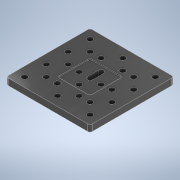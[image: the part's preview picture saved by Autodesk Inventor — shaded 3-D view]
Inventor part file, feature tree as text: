
AUTODESK INVENTOR PART (.ipt)
format: ipt  version: 2022 (Build 260153000, 153)  size: 283,136 bytes
history: native  units: mm
features: sketch x5, extrude x4, projected_geometry x1
ambient origin geometry x8: Origin, YZ Plane, XZ Plane, XY Plane, X Axis, Y Axis, Z Axis, Center Point
bodies: Solid1 (feature_tree)
feature tree (10):
  extrude  "Extrusion1"  Depth=77.0mm
  extrude  "Extrusion2"  Depth=8.5mm
  extrude  "Extrusion3"  Depth=20.0mm
  extrude  "Extrusion4"  Depth=5.0mm
  sketch  "Sketch5"  dims[d8=5.0mm d9=5.0mm d10=5.0mm d11=30.0mm d12=30.0mm d13=20.0mm d14=20.0mm d15=5.0mm d16=5.0mm d17=5.0mm d18=18.5mm d19=18.5mm d20=18.5mm d21=18.5mm d22=18.5mm d23=18.5mm d24=5.0mm d25=5.0mm d26=10.0mm d27=10.0mm d28=10.0mm d29=5.0mm d30=5.0mm d31=20.0mm d32=5.0mm d33=5.0mm d34=5.0mm d35=2.0mm d36=2.0mm d37=6.0mm d38=0.0mm d39=23.5mm d40=23.5mm d41=23.5mm d42=23.5mm d43=2.0mm d44=1.0mm d45=0.0mm d46=15.0mm d47=0.0mm d49=15.0mm d50=8.0mm d51=22.0mm d52=0.0mm d53=7.0mm d54=0.872665mm d55=0.5mm d56=0.872665mm]
  sketch  "Sketch1"  dims[d0=77.0mm d1=77.0mm]
  sketch  "Sketch2"  dims[d2=8.5mm d3=8.5mm]
  sketch  "Sketch3"  dims[d4=20.0mm d5=20.0mm]
  sketch  "Sketch4"  dims[d6=20.0mm d7=5.0mm]
  projected_geometry  "Projected Loop1"
